# Revit family: Haworth_Epure_MeetingTableDesk_AP_PRELIMINARY
name_source: partatom
category: Furniture
units: mm (PartAtom-declared; Revit-internal decimal feet)

## family parameters
Always vertical = Yes
Cut with Voids When Loaded = No
OmniClass Number = 23.40.70.14.64.11
OmniClass Title = Office Furniture
Room Calculation Point = No
Shared = No
Work Plane-Based = No

## types (4) — shared parameters
Actual Height = 730 mm  [stored 2.39501 ft]
Assembly Code = E2020200
Depth = 700 mm
Description = Haworth - Epure -Meeting Table Desk
Flip Top Finish = Haworth _ Paint _ Metallic Silver
Leg Height = 695 mm  [stored 2.28018 ft]
Manufacturer = Haworth
Model = SYEPMT1X
Revision Number = 1
Size = Verify Final Dim.w/ Haworth
Trim Finish = Haworth _ Metal _ Structured White EC
URL = https://www.haworth.com
URL - Product = https://www.haworth.com
Warranty = http://www.haworth.com
Wooden Legs A1 = No
Wooden Legs A2 = No
Wooden Legs Drop Table = No
Worksurface Dimension = 1490 x 1490, 1090 x 1090, 1200dia, 1100dia

## per-type parameters (varying)
| type | Accessory Kit | Actual Depth | Actual Width | Aluminium Legs | Aluminium Legs A1 | Aluminium Legs A2 | Aluminium Legs Drop Table | Large Drop Table | Large Round Table | No Accessory Kit | Round Cable Outlet | Small Drop Table | Small Round Table | Umbilical Cord | Wooden Legs |
| 1490 x 1490 | No | 1490 mm | 1490 mm | No | No | No | Yes | Yes | No | Yes | No | No | No | No | Yes |
| 1090 x 1090 | No | 1090 mm | 1090 mm | Yes | No | No | Yes | No | No | Yes | No | Yes | No | No | No |
| 1200 x 1200 | Yes | 1200 mm | 1200 mm | Yes | Yes | Yes | No | No | Yes | No | Yes | No | No | Yes | No |
| 1100 x 1100 | Yes | 1100 mm | 1100 mm | No | Yes | Yes | No | No | No | No | Yes | No | Yes | No | Yes |

note: [stored X ft] marks values corroborated as IEEE doubles in the binary element streams (Revit-internal decimal feet)

## geometry (parser evidence)
native form markers: Sweep x16
no freeform markers — native parametric forms only
